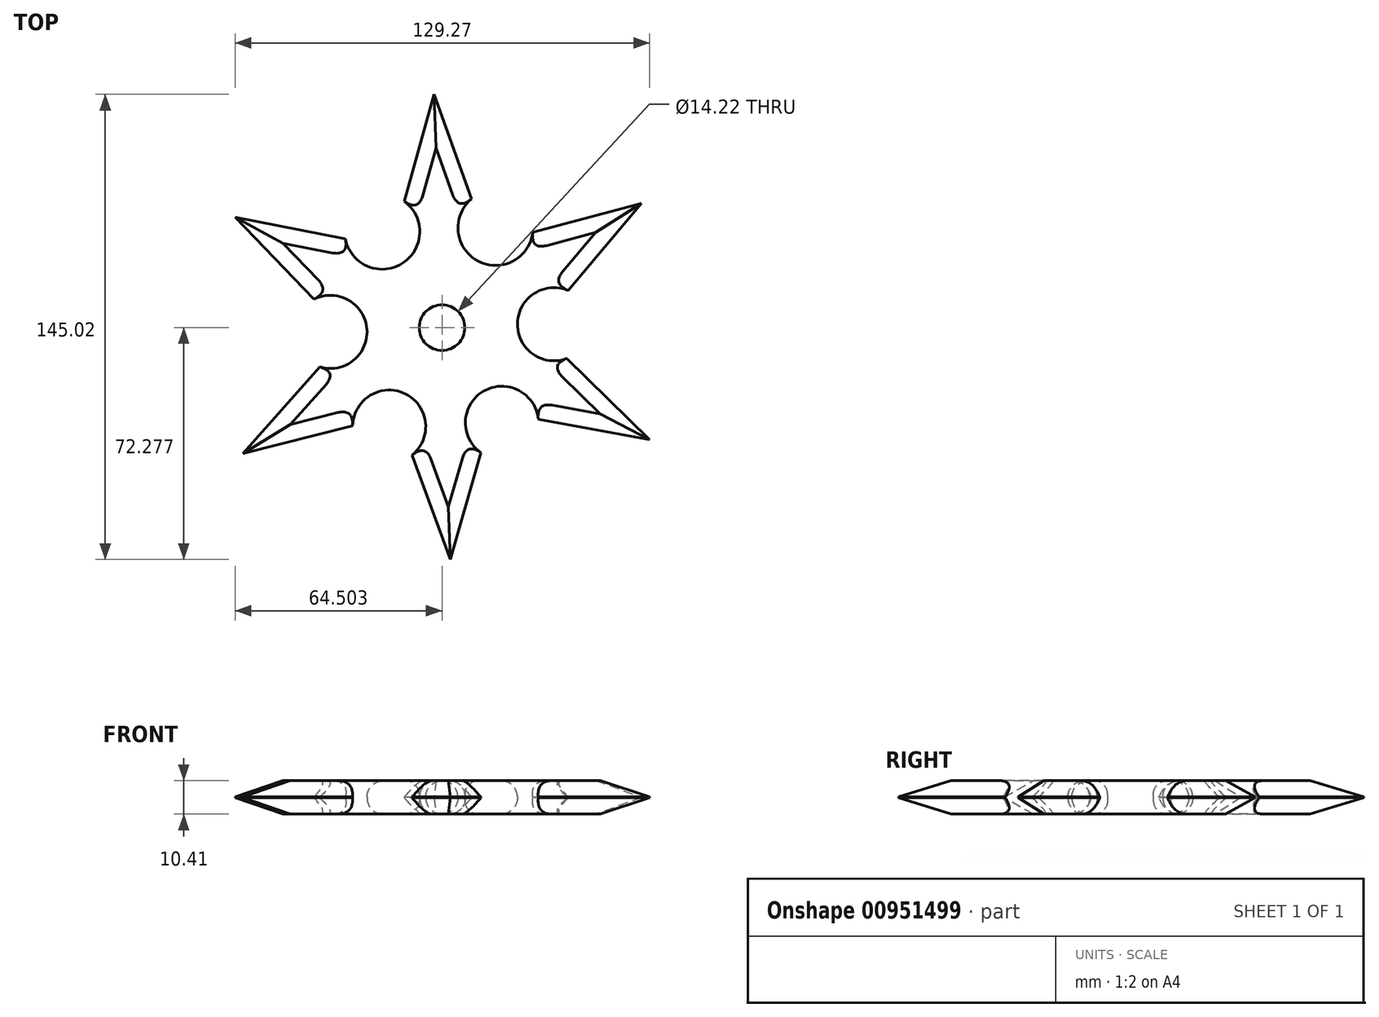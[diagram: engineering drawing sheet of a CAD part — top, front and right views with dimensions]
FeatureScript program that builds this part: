
annotation { "Feature Type Name" : "Feature", "Feature Type Description" : "" }
export const myFeature = defineFeature(function(context is Context, id is Id, definition is map)
    precondition{}
    {
        {
            var Q0;
            Q0=qCreatedBy(makeId("Top.planeOp"),FACE);
            var sketch = newSketch(context, id + "F0", { "sketchPlane" : qUnion([Q0])});
            skLineSegment(sketch, "E0", {"start": v(30.32, 57.74) * mm, "end": v(20.97, 24.39) * mm});
            skLineSegment(sketch, "E1", {"start": v(-31.76, 19.43) * mm, "end": v(2.62, 12.7) * mm});
            skLineSegment(sketch, "E2", {"start": v(-31.76, 19.43) * mm, "end": v(-7.14, -6.12) * mm});
            skArc(sketch, "E3", {"start": v(2.62, 12.7) * mm, "mid": v(20.4, 5.04) * mm, "end": v(20.97, 24.39) * mm});
            skArc(sketch, "E4", {"start": v(-5.34, -27.25) * mm, "mid": v(9.34, -15.36) * mm, "end": v(-7.14, -6.12) * mm});
            skLineSegment(sketch, "E5", {"start": v(-5.34, -27.25) * mm, "end": v(-29.33, -54.3) * mm});
            skLineSegment(sketch, "E6", {"start": v(-29.33, -54.3) * mm, "end": v(4.9, -45.57) * mm});
            skArc(sketch, "E7", {"start": v(23.45, -54.73) * mm, "mid": v(21.33, -35.66) * mm, "end": v(4.9, -45.57) * mm});
            skLineSegment(sketch, "E8", {"start": v(23.45, -54.73) * mm, "end": v(35.3, -87.28) * mm});
            skLineSegment(sketch, "E9.MirrorCS", {"start": v(30.32, 57.74) * mm, "end": v(41.94, 25.1) * mm});
            skArc(sketch, "E10.MirrorCS", {"start": v(61.04, 14.7) * mm, "mid": v(43.83, 5.84) * mm, "end": v(41.94, 25.1) * mm});
            skLineSegment(sketch, "E11.MirrorCS", {"start": v(94.88, 23.77) * mm, "end": v(61.04, 14.7) * mm});
            skLineSegment(sketch, "E12.MirrorCS", {"start": v(94.88, 23.77) * mm, "end": v(72.07, -3.4) * mm});
            skArc(sketch, "E13.MirrorCS", {"start": v(71.72, -24.6) * mm, "mid": v(56.26, -13.75) * mm, "end": v(72.07, -3.4) * mm});
            skLineSegment(sketch, "E14.MirrorCS", {"start": v(71.72, -24.6) * mm, "end": v(97.5, -49.94) * mm});
            skLineSegment(sketch, "E15.MirrorCS", {"start": v(97.5, -49.94) * mm, "end": v(62.75, -43.58) * mm});
            skArc(sketch, "E16.MirrorCS", {"start": v(44.88, -54) * mm, "mid": v(45.68, -34.83) * mm, "end": v(62.75, -43.58) * mm});
            skLineSegment(sketch, "E17.MirrorCS", {"start": v(44.88, -54) * mm, "end": v(35.3, -87.28) * mm});
            skCircle(sketch, "E18", {"center": v(32.74, -15) * mm, "radius": 7.1 * mm});
            skSolve(sketch);
        }
        {
            var Q0;
            Q0=makeQuery(id+"F0.imprint","IMPRINT",FACE,{"disambiguationData":[TD([[makeQuery(id+"F0.imprint","IMPRINT",EDGE,{"derivedFrom":sQuery(id+"F0.wireOp",EDGE,"E0")}),1.0]])]});
            extrude(context, id + "F1", {"entities" : qUnion([Q0]), "depth" : 10.4 * mm, "offsetDistance" : 25.4 * mm});
        }
        {
            var Q0;
            Q0=makeQuery(id+"F1.opExtrude","CAP_EDGE",EDGE,{"disambiguationData":[OSD([sQuery(id+"F0.wireOp",EDGE,"E5")])],"isStart":false});
            var Q1;
            Q1=makeQuery(id+"F1.opExtrude","CAP_EDGE",EDGE,{"disambiguationData":[OSD([sQuery(id+"F0.wireOp",EDGE,"E6")])],"isStart":false});
            var Q2;
            Q2=makeQuery(id+"F1.opExtrude","CAP_EDGE",EDGE,{"disambiguationData":[OSD([sQuery(id+"F0.wireOp",EDGE,"E8")])],"isStart":false});
            var Q3;
            Q3=makeQuery(id+"F1.opExtrude","CAP_EDGE",EDGE,{"disambiguationData":[OSD([sQuery(id+"F0.wireOp",EDGE,"E17.MirrorCS")])],"isStart":false});
            var Q4;
            Q4=makeQuery(id+"F1.opExtrude","CAP_EDGE",EDGE,{"disambiguationData":[OSD([sQuery(id+"F0.wireOp",EDGE,"E15.MirrorCS")])],"isStart":false});
            var Q5;
            Q5=makeQuery(id+"F1.opExtrude","CAP_EDGE",EDGE,{"disambiguationData":[OSD([sQuery(id+"F0.wireOp",EDGE,"E14.MirrorCS")])],"isStart":false});
            var Q6;
            Q6=makeQuery(id+"F1.opExtrude","CAP_EDGE",EDGE,{"disambiguationData":[OSD([sQuery(id+"F0.wireOp",EDGE,"E12.MirrorCS")])],"isStart":false});
            var Q7;
            Q7=makeQuery(id+"F1.opExtrude","CAP_EDGE",EDGE,{"disambiguationData":[OSD([sQuery(id+"F0.wireOp",EDGE,"E11.MirrorCS")])],"isStart":false});
            var Q8;
            Q8=makeQuery(id+"F1.opExtrude","CAP_EDGE",EDGE,{"disambiguationData":[OSD([sQuery(id+"F0.wireOp",EDGE,"E9.MirrorCS")])],"isStart":false});
            var Q9;
            Q9=makeQuery(id+"F1.opExtrude","CAP_EDGE",EDGE,{"disambiguationData":[OSD([sQuery(id+"F0.wireOp",EDGE,"E0")])],"isStart":false});
            var Q10;
            Q10=makeQuery(id+"F1.opExtrude","CAP_EDGE",EDGE,{"disambiguationData":[OSD([sQuery(id+"F0.wireOp",EDGE,"E1")])],"isStart":false});
            var Q11;
            Q11=makeQuery(id+"F1.opExtrude","CAP_EDGE",EDGE,{"disambiguationData":[OSD([sQuery(id+"F0.wireOp",EDGE,"E2")])],"isStart":false});
            var Q12;
            Q12=makeQuery(id+"F1.opExtrude","CAP_EDGE",EDGE,{"disambiguationData":[OSD([sQuery(id+"F0.wireOp",EDGE,"E1")])],"isStart":true});
            var Q13;
            Q13=makeQuery(id+"F1.opExtrude","CAP_EDGE",EDGE,{"disambiguationData":[OSD([sQuery(id+"F0.wireOp",EDGE,"E2")])],"isStart":true});
            var Q14;
            Q14=makeQuery(id+"F1.opExtrude","CAP_EDGE",EDGE,{"disambiguationData":[OSD([sQuery(id+"F0.wireOp",EDGE,"E5")])],"isStart":true});
            var Q15;
            Q15=makeQuery(id+"F1.opExtrude","CAP_EDGE",EDGE,{"disambiguationData":[OSD([sQuery(id+"F0.wireOp",EDGE,"E6")])],"isStart":true});
            var Q16;
            Q16=makeQuery(id+"F1.opExtrude","CAP_EDGE",EDGE,{"disambiguationData":[OSD([sQuery(id+"F0.wireOp",EDGE,"E8")])],"isStart":true});
            var Q17;
            Q17=makeQuery(id+"F1.opExtrude","CAP_EDGE",EDGE,{"disambiguationData":[OSD([sQuery(id+"F0.wireOp",EDGE,"E17.MirrorCS")])],"isStart":true});
            var Q18;
            Q18=makeQuery(id+"F1.opExtrude","CAP_EDGE",EDGE,{"disambiguationData":[OSD([sQuery(id+"F0.wireOp",EDGE,"E15.MirrorCS")])],"isStart":true});
            var Q19;
            Q19=makeQuery(id+"F1.opExtrude","CAP_EDGE",EDGE,{"disambiguationData":[OSD([sQuery(id+"F0.wireOp",EDGE,"E14.MirrorCS")])],"isStart":true});
            var Q20;
            Q20=makeQuery(id+"F1.opExtrude","CAP_EDGE",EDGE,{"disambiguationData":[OSD([sQuery(id+"F0.wireOp",EDGE,"E12.MirrorCS")])],"isStart":true});
            var Q21;
            Q21=makeQuery(id+"F1.opExtrude","CAP_EDGE",EDGE,{"disambiguationData":[OSD([sQuery(id+"F0.wireOp",EDGE,"E11.MirrorCS")])],"isStart":true});
            var Q22;
            Q22=makeQuery(id+"F1.opExtrude","CAP_EDGE",EDGE,{"disambiguationData":[OSD([sQuery(id+"F0.wireOp",EDGE,"E0")])],"isStart":true});
            var Q23;
            Q23=makeQuery(id+"F1.opExtrude","CAP_EDGE",EDGE,{"disambiguationData":[OSD([sQuery(id+"F0.wireOp",EDGE,"E9.MirrorCS")])],"isStart":true});
            chamfer(context, id + "F2", {"entities" : qUnion([Q0, Q1, Q2, Q3, Q4, Q5, Q6, Q7, Q8, Q9, Q10, Q11, Q12, Q13, Q14, Q15, Q16, Q17, Q18, Q19, Q20, Q21, Q22, Q23]), "width" : 5.08 * mm, "tangentPropagation" : true});
        }
        {
            var Q0;
            Q0=makeQuery(id+"F1.opExtrude","CAP_EDGE",EDGE,{"disambiguationData":[OSD([sQuery(id+"F0.wireOp",EDGE,"E13.MirrorCS")])],"isStart":false});
            var Q1;
            Q1=makeQuery(id+"F1.opExtrude","CAP_EDGE",EDGE,{"disambiguationData":[OSD([sQuery(id+"F0.wireOp",EDGE,"E16.MirrorCS")])],"isStart":false});
            var Q2;
            Q2=makeQuery(id+"F1.opExtrude","CAP_EDGE",EDGE,{"disambiguationData":[OSD([sQuery(id+"F0.wireOp",EDGE,"E7")])],"isStart":false});
            var Q3;
            Q3=makeQuery(id+"F1.opExtrude","CAP_EDGE",EDGE,{"disambiguationData":[OSD([sQuery(id+"F0.wireOp",EDGE,"E4")])],"isStart":false});
            var Q4;
            Q4=makeQuery(id+"F1.opExtrude","CAP_EDGE",EDGE,{"disambiguationData":[OSD([sQuery(id+"F0.wireOp",EDGE,"E3")])],"isStart":false});
            var Q5;
            Q5=makeQuery(id+"F1.opExtrude","CAP_EDGE",EDGE,{"disambiguationData":[OSD([sQuery(id+"F0.wireOp",EDGE,"E10.MirrorCS")])],"isStart":false});
            var Q6;
            Q6=makeQuery(id+"F1.opExtrude","CAP_EDGE",EDGE,{"disambiguationData":[OSD([sQuery(id+"F0.wireOp",EDGE,"E10.MirrorCS")])],"isStart":true});
            var Q7;
            Q7=makeQuery(id+"F1.opExtrude","CAP_EDGE",EDGE,{"disambiguationData":[OSD([sQuery(id+"F0.wireOp",EDGE,"E13.MirrorCS")])],"isStart":true});
            var Q8;
            Q8=makeQuery(id+"F1.opExtrude","CAP_EDGE",EDGE,{"disambiguationData":[OSD([sQuery(id+"F0.wireOp",EDGE,"E16.MirrorCS")])],"isStart":true});
            var Q9;
            Q9=makeQuery(id+"F1.opExtrude","CAP_EDGE",EDGE,{"disambiguationData":[OSD([sQuery(id+"F0.wireOp",EDGE,"E7")])],"isStart":true});
            var Q10;
            Q10=makeQuery(id+"F1.opExtrude","CAP_EDGE",EDGE,{"disambiguationData":[OSD([sQuery(id+"F0.wireOp",EDGE,"E4")])],"isStart":true});
            var Q11;
            Q11=makeQuery(id+"F1.opExtrude","CAP_EDGE",EDGE,{"disambiguationData":[OSD([sQuery(id+"F0.wireOp",EDGE,"E3")])],"isStart":true});
            fillet(context, id + "F3", {"entities" : qUnion([Q0, Q1, Q2, Q3, Q4, Q5, Q6, Q7, Q8, Q9, Q10, Q11]), "radius" : 5.08 * mm, "tangentPropagation" : true, "allowEdgeOverflow" : false});
        }
        {
            var Q0;
            Q0=makeQuery(id+"F1.opExtrude","CAP_EDGE",EDGE,{"disambiguationData":[OSD([sQuery(id+"F0.wireOp",EDGE,"E18")])],"isStart":true});
            var Q1;
            Q1=makeQuery(id+"F1.opExtrude","CAP_EDGE",EDGE,{"disambiguationData":[OSD([sQuery(id+"F0.wireOp",EDGE,"E18")])],"isStart":false});
            fillet(context, id + "F4", {"entities" : qUnion([Q0, Q1]), "radius" : 4.3 * mm, "tangentPropagation" : true, "allowEdgeOverflow" : false});
        }
    });
